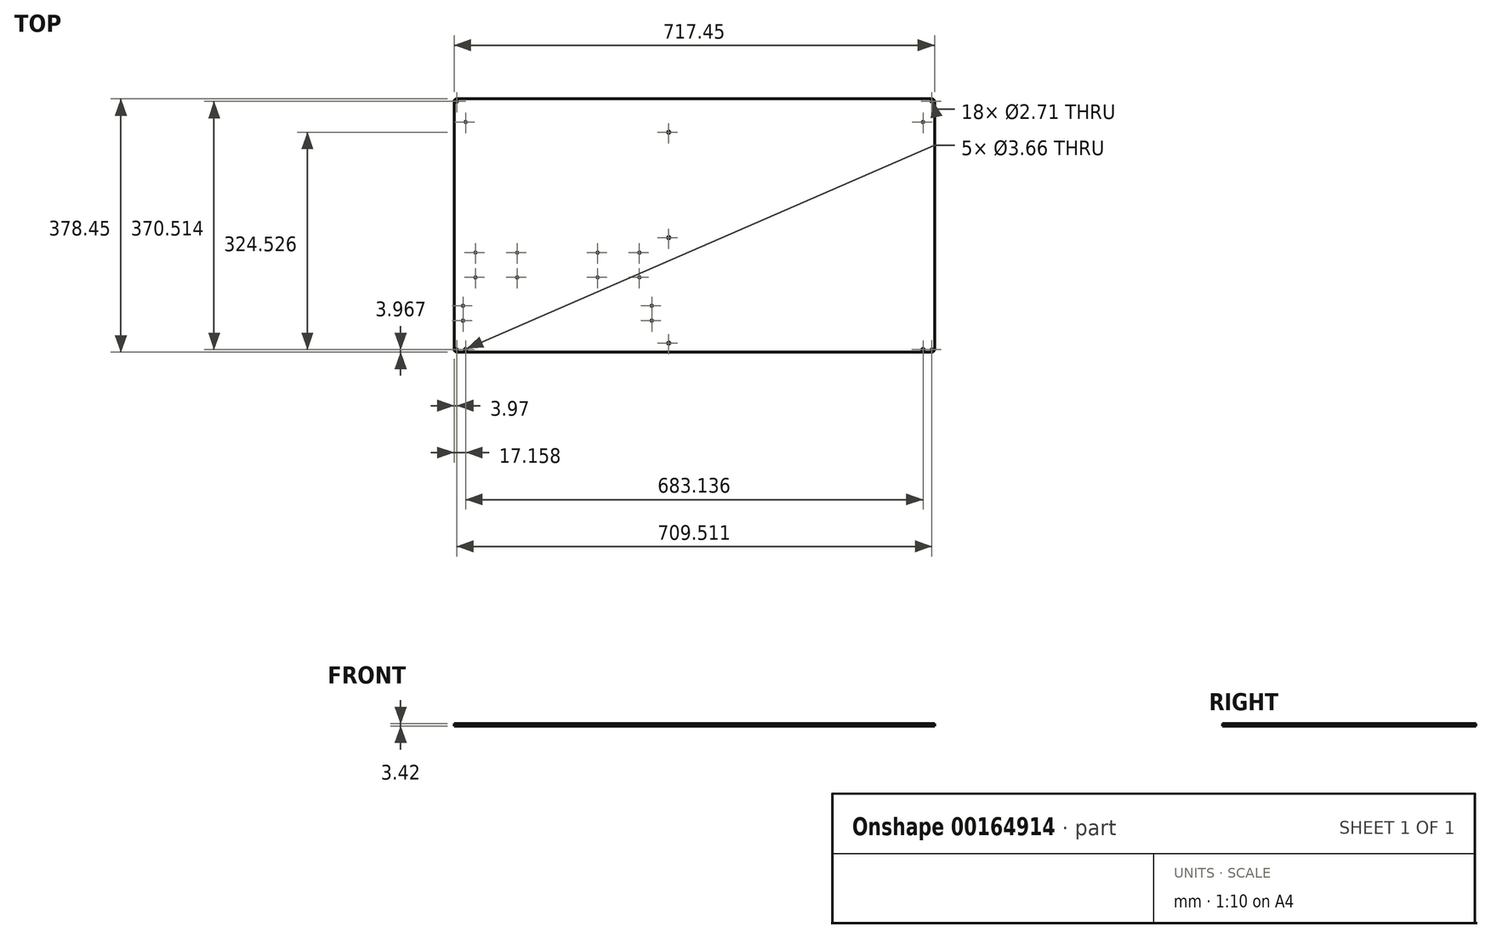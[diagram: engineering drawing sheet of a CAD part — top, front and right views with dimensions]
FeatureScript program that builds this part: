
annotation { "Feature Type Name" : "Feature", "Feature Type Description" : "" }
export const myFeature = defineFeature(function(context is Context, id is Id, definition is map)
    precondition{}
    {
        {
            var Q0;
            Q0=qCreatedBy(makeId("Top.planeOp"),FACE);
            var sketch = newSketch(context, id + "F0", { "sketchPlane" : qUnion([Q0])});
            skLineSegment(sketch, "E0.bottom", {"start": v(0, 0) * mm, "end": v(-717.45, 0) * mm});
            skLineSegment(sketch, "E0.top", {"start": v(0, -378.45) * mm, "end": v(-717.45, -378.45) * mm});
            skLineSegment(sketch, "E0.left", {"start": v(0, 0) * mm, "end": v(0, -378.45) * mm});
            skLineSegment(sketch, "E0.right", {"start": v(-717.45, 0) * mm, "end": v(-717.45, -378.45) * mm});
            skSolve(sketch);
        }
        {
            var Q0;
            Q0 = qSketchRegion(id + "F0", true);
            extrude(context, id + "F1", {"entities" : qUnion([Q0]), "depth" : 3.42 * mm});
        }
        {
            var Q0;
            Q0=makeQuery(id+"F1.opExtrude","SWEPT_EDGE",EDGE,{"disambiguationData":[OSD([sQuery(id+"F0.wireOp",EDGE,"E0.bottom"),sQuery(id+"F0.wireOp",EDGE,"E0.right")])]});
            var Q1;
            Q1=makeQuery(id+"F1.opExtrude","SWEPT_EDGE",EDGE,{"disambiguationData":[OSD([sQuery(id+"F0.wireOp",EDGE,"E0.top"),sQuery(id+"F0.wireOp",EDGE,"E0.right")])]});
            var Q2;
            Q2=makeQuery(id+"F1.opExtrude","SWEPT_EDGE",EDGE,{"disambiguationData":[OSD([sQuery(id+"F0.wireOp",EDGE,"E0.top"),sQuery(id+"F0.wireOp",EDGE,"E0.left")])]});
            var Q3;
            Q3=makeQuery(id+"F1.opExtrude","SWEPT_EDGE",EDGE,{"disambiguationData":[OSD([sQuery(id+"F0.wireOp",EDGE,"E0.bottom"),sQuery(id+"F0.wireOp",EDGE,"E0.left")])]});
            fillet(context, id + "F2", {"entities" : qUnion([Q0, Q1, Q2, Q3]), "radius" : 3.97 * mm, "tangentPropagation" : true, "allowEdgeOverflow" : false});
        }
        {
            var Q0;
            Q0=makeQuery(id+"F1.opExtrude","CAP_FACE",FACE,{"disambiguationData":[OSD([sQuery(id+"F0.wireOp",EDGE,"E0.bottom"),sQuery(id+"F0.wireOp",EDGE,"E0.top"),sQuery(id+"F0.wireOp",EDGE,"E0.left"),sQuery(id+"F0.wireOp",EDGE,"E0.right")])],"isStart":false});
            var sketch = newSketch(context, id + "F3", { "sketchPlane" : qUnion([Q0])});
            skCircle(sketch, "E1", {"center": v(-713.48, -3.97) * mm, "radius": 1.35 * mm});
            skCircle(sketch, "E2", {"center": v(-3.97, -3.97) * mm, "radius": 1.35 * mm});
            skCircle(sketch, "E3", {"center": v(-713.48, -374.48) * mm, "radius": 1.35 * mm});
            skCircle(sketch, "E4", {"center": v(-3.97, -374.48) * mm, "radius": 1.35 * mm});
            skLineSegment(sketch, "E5", {"start": v(-422.2, -320.25) * mm, "end": v(-704.15, -320.25) * mm, "construction": true});
            skLineSegment(sketch, "E6", {"start": v(-422.2, -309.1) * mm, "end": v(-422.2, -331.4) * mm, "construction": true});
            skLineSegment(sketch, "E7", {"start": v(-704.15, -309.1) * mm, "end": v(-704.15, -331.4) * mm, "construction": true});
            skCircle(sketch, "E8", {"center": v(-704.15, -309.1) * mm, "radius": 1.35 * mm});
            skCircle(sketch, "E9", {"center": v(-704.15, -331.4) * mm, "radius": 1.35 * mm});
            skCircle(sketch, "E10", {"center": v(-422.2, -331.4) * mm, "radius": 1.35 * mm});
            skCircle(sketch, "E11", {"center": v(-422.2, -309.1) * mm, "radius": 1.35 * mm});
            skLineSegment(sketch, "E12", {"start": v(-563.18, -320.25) * mm, "end": v(-563.18, -378.45) * mm, "construction": true});
            skLineSegment(sketch, "E13", {"start": v(-3.97, -374.48) * mm, "end": v(-17.16, -374.48) * mm, "construction": true});
            skLineSegment(sketch, "E14", {"start": v(-713.48, -374.48) * mm, "end": v(-700.3, -374.48) * mm, "construction": true});
            skCircle(sketch, "E15", {"center": v(-17.16, -374.48) * mm, "radius": 1.83 * mm});
            skCircle(sketch, "E16", {"center": v(-700.3, -374.48) * mm, "radius": 1.83 * mm});
            skLineSegment(sketch, "E17", {"start": v(-422.2, -309.1) * mm, "end": v(-422.2, -248.23) * mm, "construction": true});
            skLineSegment(sketch, "E18", {"start": v(-422.2, -248.23) * mm, "end": v(-471.92, -248.23) * mm, "construction": true});
            skLineSegment(sketch, "E19.bottom", {"start": v(-503.07, -266.75) * mm, "end": v(-440.78, -266.75) * mm, "construction": true});
            skLineSegment(sketch, "E19.top", {"start": v(-503.07, -229.7) * mm, "end": v(-440.78, -229.7) * mm, "construction": true});
            skLineSegment(sketch, "E19.left", {"start": v(-503.07, -266.75) * mm, "end": v(-503.07, -229.7) * mm, "construction": true});
            skLineSegment(sketch, "E19.right", {"start": v(-440.78, -266.75) * mm, "end": v(-440.78, -229.7) * mm, "construction": true});
            skPoint(sketch, "E19.middle", {"position": v(-471.92, -248.23) * mm});
            skCircle(sketch, "E20", {"center": v(-440.78, -266.75) * mm, "radius": 1.35 * mm});
            skCircle(sketch, "E21", {"center": v(-440.78, -229.7) * mm, "radius": 1.35 * mm});
            skCircle(sketch, "E22", {"center": v(-503.07, -229.7) * mm, "radius": 1.35 * mm});
            skCircle(sketch, "E23", {"center": v(-503.07, -266.75) * mm, "radius": 1.35 * mm});
            skLineSegment(sketch, "E24", {"start": v(-704.15, -309.1) * mm, "end": v(-704.15, -248.23) * mm, "construction": true});
            skLineSegment(sketch, "E25", {"start": v(-704.15, -248.23) * mm, "end": v(-654.43, -248.23) * mm, "construction": true});
            skLineSegment(sketch, "E26.bottom", {"start": v(-623.28, -266.75) * mm, "end": v(-685.57, -266.75) * mm, "construction": true});
            skLineSegment(sketch, "E26.top", {"start": v(-623.28, -229.7) * mm, "end": v(-685.57, -229.7) * mm, "construction": true});
            skLineSegment(sketch, "E26.left", {"start": v(-623.28, -266.75) * mm, "end": v(-623.28, -229.7) * mm, "construction": true});
            skLineSegment(sketch, "E26.right", {"start": v(-685.57, -266.75) * mm, "end": v(-685.57, -229.7) * mm, "construction": true});
            skPoint(sketch, "E26.middle", {"position": v(-654.43, -248.23) * mm});
            skLineSegment(sketch, "E27", {"start": v(-358.72, 0) * mm, "end": v(-358.72, -34.63) * mm, "construction": true});
            skLineSegment(sketch, "E28", {"start": v(-700.3, -34.63) * mm, "end": v(-17.16, -34.63) * mm, "construction": true});
            skCircle(sketch, "E29", {"center": v(-700.3, -34.63) * mm, "radius": 1.35 * mm});
            skCircle(sketch, "E30", {"center": v(-17.16, -34.63) * mm, "radius": 1.35 * mm});
            skCircle(sketch, "E31", {"center": v(-623.28, -266.75) * mm, "radius": 1.35 * mm});
            skCircle(sketch, "E32", {"center": v(-623.28, -229.7) * mm, "radius": 1.35 * mm});
            skCircle(sketch, "E33", {"center": v(-685.57, -229.7) * mm, "radius": 1.35 * mm});
            skCircle(sketch, "E34", {"center": v(-685.57, -266.75) * mm, "radius": 1.35 * mm});
            skLineSegment(sketch, "E35", {"start": v(-397, -34.63) * mm, "end": v(-397, -49.96) * mm, "construction": true});
            skLineSegment(sketch, "E36", {"start": v(-397, -49.96) * mm, "end": v(-422.2, -49.96) * mm, "construction": true});
            skLineSegment(sketch, "E37", {"start": v(-422.2, -248.23) * mm, "end": v(-422.2, -49.96) * mm, "construction": true});
            skCircle(sketch, "E38", {"center": v(-397, -49.96) * mm, "radius": 1.83 * mm});
            skLineSegment(sketch, "E39", {"start": v(-397, -49.96) * mm, "end": v(-397, -364.96) * mm, "construction": true});
            skCircle(sketch, "E40", {"center": v(-397, -364.96) * mm, "radius": 1.83 * mm});
            skCircle(sketch, "E41", {"center": v(-397, -207.46) * mm, "radius": 1.83 * mm});
            skSolve(sketch);
        }
        {
            var Q0;
            Q0 = qSketchRegion(id + "F3", true);
            var Q1;
            Q1=makeQuery(id+"F1.opExtrude","CAP_FACE",FACE,{"disambiguationData":[OSD([sQuery(id+"F0.wireOp",EDGE,"E0.bottom"),sQuery(id+"F0.wireOp",EDGE,"E0.top"),sQuery(id+"F0.wireOp",EDGE,"E0.left"),sQuery(id+"F0.wireOp",EDGE,"E0.right")])],"isStart":true});
            extrude(context, id + "F4", {"entities" : qUnion([Q0]), "operationType" : NewBodyOperationType.REMOVE, "endBound" : BoundingType.UP_TO_SURFACE, "oppositeDirection" : true, "endBoundEntityFace" : qUnion([Q1]), "depth" : 25.4 * mm});
        }
    });
